# Revit family: Magnuson-Kaskad-End_Ext_Planter
name_source: partatom
category: Furniture
units: mm (PartAtom-declared; Revit-internal decimal feet)

## family parameters
Always vertical = Yes
Cut with Voids When Loaded = No
OmniClass Number = 23.40.20.00
OmniClass Title = General Furniture and Specialties
Room Calculation Point = No
Shared = No
Work Plane-Based = No

## types (1)
- KAS-R-0936H-END
    Assembly Code = E2020200
    Base Finish = MAG - Textured painted steel
    Body Finish = MAG - Textured painted steel
    Bottom Finish = MAG - Textured painted steel
    Default Elevation = 0"
    Depth = 9"
    Description = Indoor painted steel rectangular planter with one connecting side (to connect to other KASKAD END or MID units with hardware) and one side with radiused corners - for use at the end of a configuration. Includes two liners, adjustable glides and two stabilizer bases that can be used in place of adjustable glides for additional stability.
    Glides Finish = MAG - Plastic Black
    Height = 36"
    Keynote = 12500
    Liners Finish = MAG - Plastic Black
    Manufacturer = Magnuson Group
    Model = KAS-R-0936H-END
    Product Documentation Link = https://magnusongroup.com
    Revit File Built By = https://servex-us.com
    Sustainability = https://magnusongroup.com
    Type Comments = Kaskad
    URL = www.magnusongroup.com
    Width = 36"

## geometry (parser evidence)
native form markers: Sweep x2
no freeform markers — native parametric forms only
